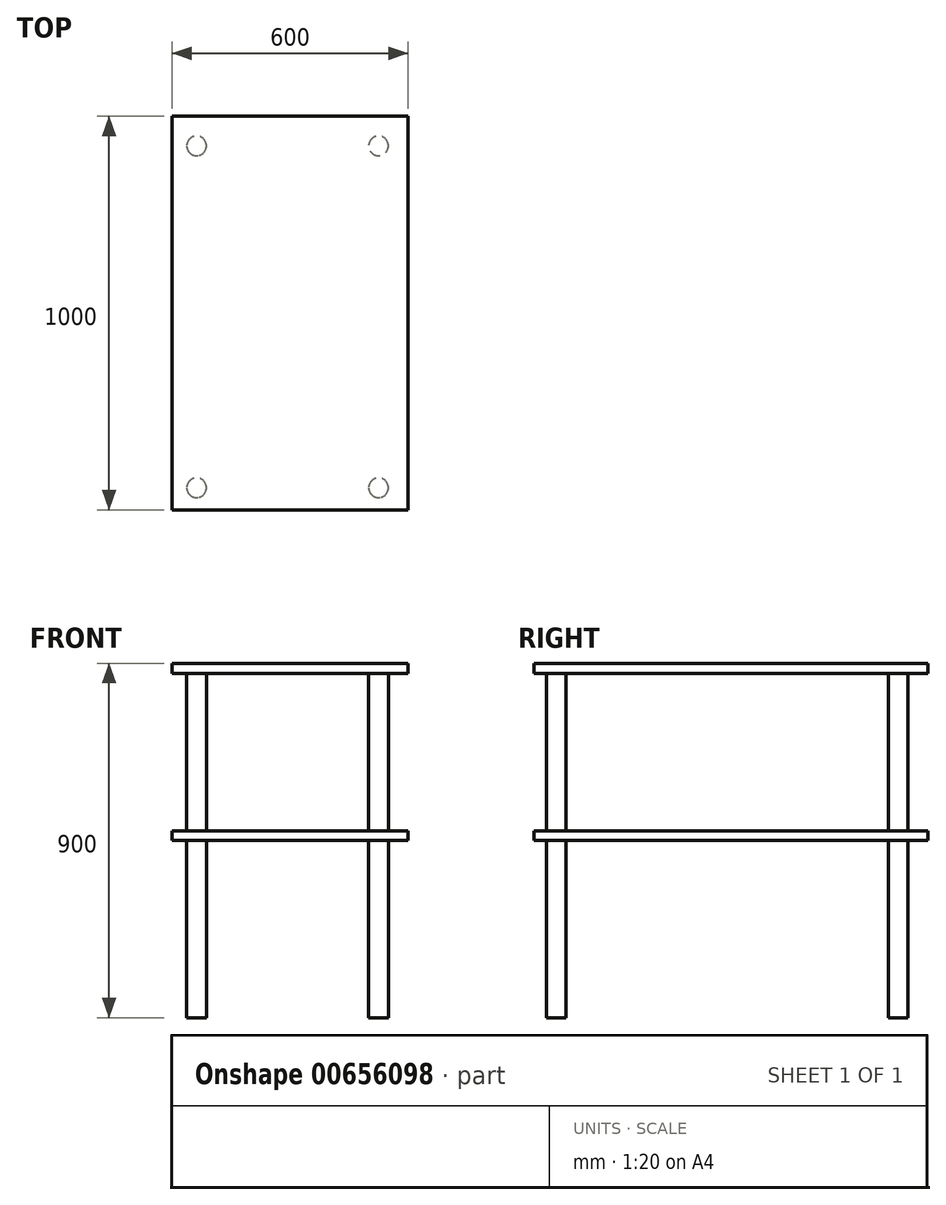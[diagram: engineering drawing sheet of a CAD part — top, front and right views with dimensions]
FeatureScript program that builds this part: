
annotation { "Feature Type Name" : "Feature", "Feature Type Description" : "" }
export const myFeature = defineFeature(function(context is Context, id is Id, definition is map)
    precondition{}
    {
        {
            var Q0;
            Q0=qCreatedBy(makeId("Front.planeOp"),FACE);
            var sketch = newSketch(context, id + "F0", { "sketchPlane" : qUnion([Q0])});
            skLineSegment(sketch, "E0.bottom", {"start": v(0, 875) * mm, "end": v(600, 875) * mm});
            skLineSegment(sketch, "E0.top", {"start": v(0, 900) * mm, "end": v(600, 900) * mm});
            skLineSegment(sketch, "E0.left", {"start": v(0, 875) * mm, "end": v(0, 900) * mm});
            skLineSegment(sketch, "E0.right", {"start": v(600, 875) * mm, "end": v(600, 900) * mm});
            skSolve(sketch);
        }
        {
            var Q0;
            Q0=makeQuery(id+"F0.imprint","IMPRINT",FACE,{"disambiguationData":[TD([[makeQuery(id+"F0.imprint","IMPRINT",EDGE,{"derivedFrom":sQuery(id+"F0.wireOp",EDGE,"E0.bottom")}),1.0]])]});
            extrude(context, id + "F1", {"entities" : qUnion([Q0]), "depth" : 1000 * mm, "offsetDistance" : 25.4 * mm});
        }
        {
            var Q0;
            Q0=makeQuery(id+"F1.opExtrude","SWEPT_FACE",FACE,{"disambiguationData":[OSD([sQuery(id+"F0.wireOp",EDGE,"E0.bottom")])]});
            var sketch = newSketch(context, id + "F2", { "sketchPlane" : qUnion([Q0])});
            skCircle(sketch, "E1", {"center": v(525, 75) * mm, "radius": 25 * mm});
            skCircle(sketch, "E2.0.1.0", {"center": v(525, 943.68) * mm, "radius": 25 * mm});
            skCircle(sketch, "E2.1.0.0", {"center": v(62.72, 75) * mm, "radius": 25 * mm});
            skCircle(sketch, "E2.1.1.0", {"center": v(62.72, 943.68) * mm, "radius": 25 * mm});
            skLineSegment(sketch, "E2.direction1", {"start": v(525, 75) * mm, "end": v(62.72, 75) * mm, "construction": true});
            skLineSegment(sketch, "E2.direction2", {"start": v(525, 75) * mm, "end": v(525, 943.68) * mm, "construction": true});
            skSolve(sketch);
        }
        {
            var Q0;
            Q0=makeQuery(id+"F2.imprint","IMPRINT",FACE,{"disambiguationData":[TD([[makeQuery(id+"F2.imprint","IMPRINT",EDGE,{"derivedFrom":sQuery(id+"F2.wireOp",EDGE,"E1")}),1.0]])]});
            var Q1;
            Q1=makeQuery(id+"F2.imprint","IMPRINT",FACE,{"disambiguationData":[TD([[makeQuery(id+"F2.imprint","IMPRINT",EDGE,{"derivedFrom":sQuery(id+"F2.wireOp",EDGE,"E2.1.0.0")}),1.0]])]});
            var Q2;
            Q2=makeQuery(id+"F2.imprint","IMPRINT",FACE,{"disambiguationData":[TD([[makeQuery(id+"F2.imprint","IMPRINT",EDGE,{"derivedFrom":sQuery(id+"F2.wireOp",EDGE,"E2.0.1.0")}),1.0]])]});
            var Q3;
            Q3=makeQuery(id+"F2.imprint","IMPRINT",FACE,{"disambiguationData":[TD([[makeQuery(id+"F2.imprint","IMPRINT",EDGE,{"derivedFrom":sQuery(id+"F2.wireOp",EDGE,"E2.1.1.0")}),1.0]])]});
            extrude(context, id + "F3", {"entities" : qUnion([Q0, Q1, Q2, Q3]), "operationType" : NewBodyOperationType.ADD, "depth" : 900 * mm - 25 * mm, "offsetDistance" : 25.4 * mm});
        }
        {
            var Q0;
            Q0=makeQuery(id+"F1.opExtrude","CAP_FACE",FACE,{"disambiguationData":[OSD([sQuery(id+"F0.wireOp",EDGE,"E0.bottom"),sQuery(id+"F0.wireOp",EDGE,"E0.top"),sQuery(id+"F0.wireOp",EDGE,"E0.left"),sQuery(id+"F0.wireOp",EDGE,"E0.right")])],"isStart":true});
            var sketch = newSketch(context, id + "F4", { "sketchPlane" : qUnion([Q0])});
            skLineSegment(sketch, "E3.bottom", {"start": v(-600, 475) * mm, "end": v(0, 475) * mm});
            skLineSegment(sketch, "E3.top", {"start": v(-600, 450) * mm, "end": v(0, 450) * mm});
            skLineSegment(sketch, "E3.left", {"start": v(-600, 475) * mm, "end": v(-600, 450) * mm});
            skLineSegment(sketch, "E3.right", {"start": v(0, 475) * mm, "end": v(0, 450) * mm});
            skSolve(sketch);
        }
        {
            var Q0;
            Q0=makeQuery(id+"F4.imprint","IMPRINT",FACE,{"disambiguationData":[TD([[makeQuery(id+"F4.imprint","IMPRINT",EDGE,{"derivedFrom":sQuery(id+"F4.wireOp",EDGE,"E3.bottom")}),-1.0]])]});
            extrude(context, id + "F5", {"entities" : qUnion([Q0]), "operationType" : NewBodyOperationType.ADD, "oppositeDirection" : true, "depth" : 1000 * mm, "offsetDistance" : 25.4 * mm});
        }
    });
